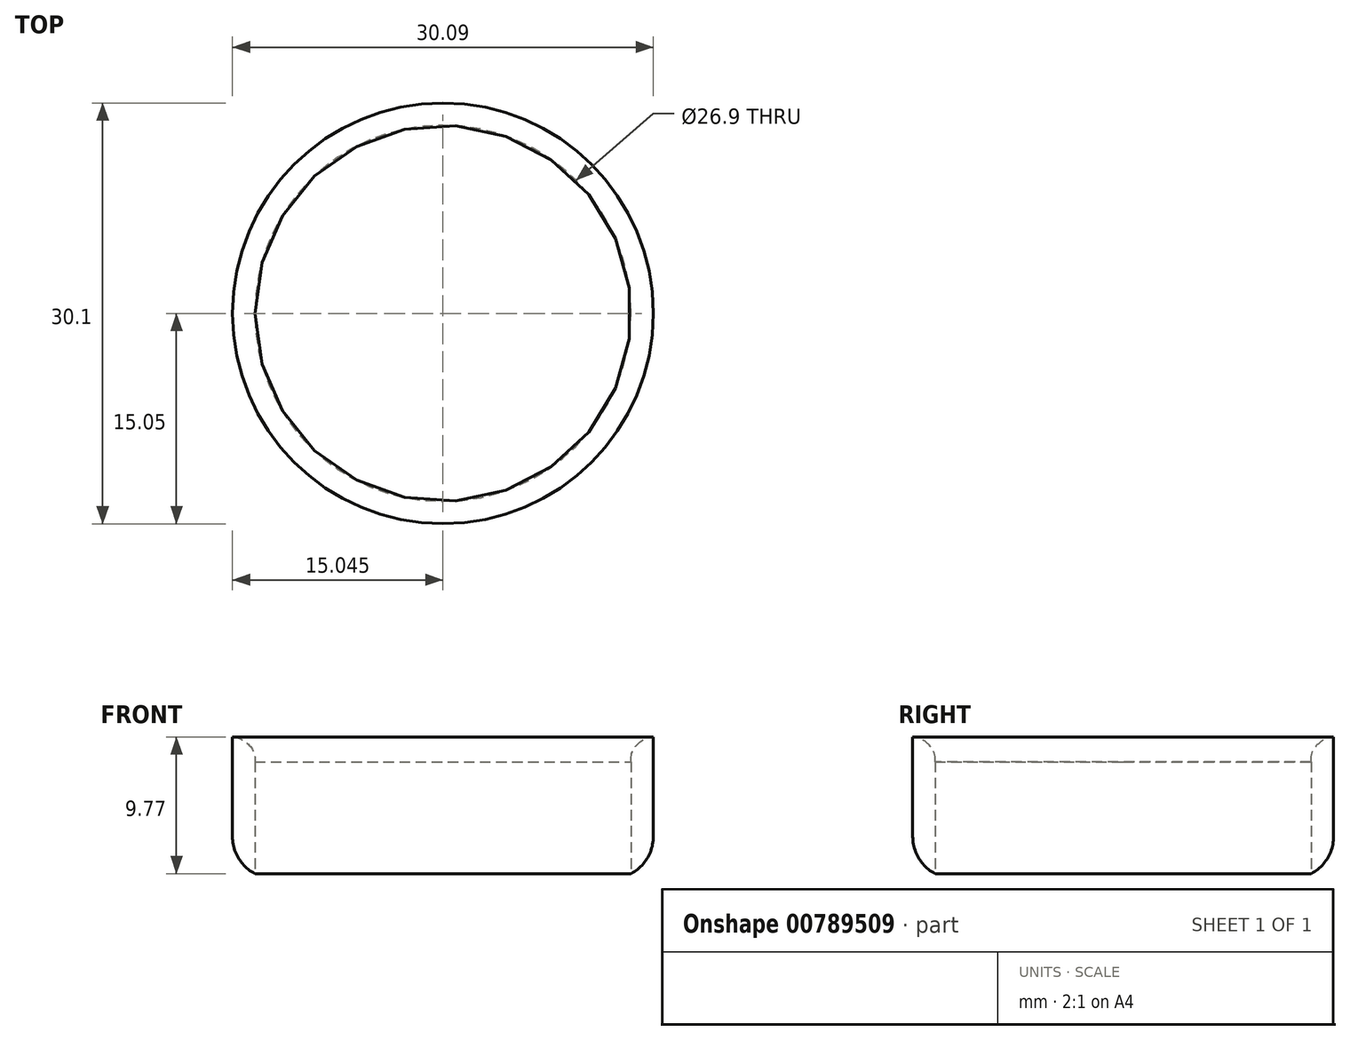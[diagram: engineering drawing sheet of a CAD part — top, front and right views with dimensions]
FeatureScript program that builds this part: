
annotation { "Feature Type Name" : "Feature", "Feature Type Description" : "" }
export const myFeature = defineFeature(function(context is Context, id is Id, definition is map)
    precondition{}
    {
        {
            var Q0;
            Q0=qCreatedBy(makeId("Front.planeOp"),FACE);
            var sketch = newSketch(context, id + "F0", { "sketchPlane" : qUnion([Q0])});
            skLineSegment(sketch, "E0", {"start": v(0, 0) * mm, "end": v(30.09, 0) * mm});
            skLineSegment(sketch, "E1", {"start": v(30.1, 0) * mm, "end": v(30.1, 8) * mm});
            skLineSegment(sketch, "E2", {"start": v(28.5, 8) * mm, "end": v(30.1, 8) * mm});
            skLineSegment(sketch, "E3", {"start": v(28.5, 8) * mm, "end": v(28.5, 0) * mm});
            skLineSegment(sketch, "E4", {"start": v(15.05, 0) * mm, "end": v(15.05, 16.56) * mm});
            skLineSegment(sketch, "E5", {"start": v(35.82, 16.56) * mm, "end": v(35.82, 11.05) * mm});
            skFitSpline(sketch, "E6", {"points": [v(30.1, 8) * mm, v(34.07, 8.82) * mm, v(35.82, 11.05) * mm], "startDerivative": vector(13.31, -0.83) * mm, "endDerivative": vector(4.49, 8.97) * mm});
            skLineSegment(sketch, "E7", {"start": v(34.25, 16.56) * mm, "end": v(35.82, 16.56) * mm});
            skPoint(sketch, "E8.orphan", {"position": v(35.82, 17.2) * mm});
            skFitSpline(sketch, "E9.0", {"points": [v(30.2, 9.75) * mm, v(30.7, 9.72) * mm, v(31.5, 9.71) * mm, v(32.24, 9.83) * mm, v(32.56, 9.94) * mm, v(32.73, 10.03) * mm, v(32.84, 10.1) * mm, v(32.92, 10.15) * mm, v(33, 10.2) * mm, v(33.14, 10.3) * mm, v(33.27, 10.4) * mm, v(33.39, 10.51) * mm, v(33.55, 10.68) * mm, v(33.8, 11) * mm, v(34.08, 11.5) * mm, v(34.25, 11.83) * mm]});
            skLineSegment(sketch, "E10", {"start": v(30.1, 8) * mm, "end": v(30.1, 9.77) * mm});
            skLineSegment(sketch, "E11", {"start": v(30.1, 9.77) * mm, "end": v(31.85, 9.77) * mm});
            skLineSegment(sketch, "E12", {"start": v(34.25, 11.83) * mm, "end": v(34.25, 16.56) * mm});
            skFitSpline(sketch, "E13", {"points": [v(30.1, 9.77) * mm, v(29.24, 9.48) * mm, v(28.67, 8.88) * mm, v(28.5, 8) * mm], "startDerivative": vector(-3.53, -0.14) * mm, "endDerivative": vector(0.31, -2.81) * mm});
            skSolve(sketch);
        }
        {
            var Q0;
            Q0=makeQuery(id+"F0.imprint","IMPRINT",FACE,{"disambiguationData":[TD([[makeQuery(id+"F0.imprint","IMPRINT",EDGE,{"derivedFrom":sQuery(id+"F0.wireOp",EDGE,"E5")}),-1.0]])]});
            var Q1;
            Q1=makeQuery(id+"F0.imprint","IMPRINT",FACE,{"disambiguationData":[TD([[makeQuery(id+"F0.imprint","IMPRINT",EDGE,{"derivedFrom":sQuery(id+"F0.wireOp",EDGE,"E2")}),1.0]])]});
            var Q2;
            {var subQ0=sQuery(id+"F0.wireOp",EDGE,"E1");Q2=makeQuery(id+"F0.imprint","IMPRINT",FACE,{"disambiguationData":[TD([[makeQuery(id+"F0.imprint","IMPRINT",EDGE,{"derivedFrom":subQ0}),1.0]])]});}
            var Q3;
            Q3=sQuery(id+"F0.wireOp",EDGE,"E4");
            revolve(context, id + "F1", {"surfaceOperationType" : NewSurfaceOperationType.NEW, "entities" : qUnion([Q0, Q1, Q2]), "axis" : qUnion([Q3]), "revolveType" : RevolveType.FULL});
        }
        {
            var Q0;
            Q0=makeQuery(id+"F1.opRevolve","SWEPT_EDGE",EDGE,{"disambiguationData":[OSD([sQuery(id+"F0.wireOp",EDGE,"E0"),sQuery(id+"F0.wireOp",EDGE,"E1")])]});
            fillet(context, id + "F2", {"entities" : qUnion([Q0]), "radius" : 3 * mm, "tangentPropagation" : true, "allowEdgeOverflow" : false});
        }
    });
